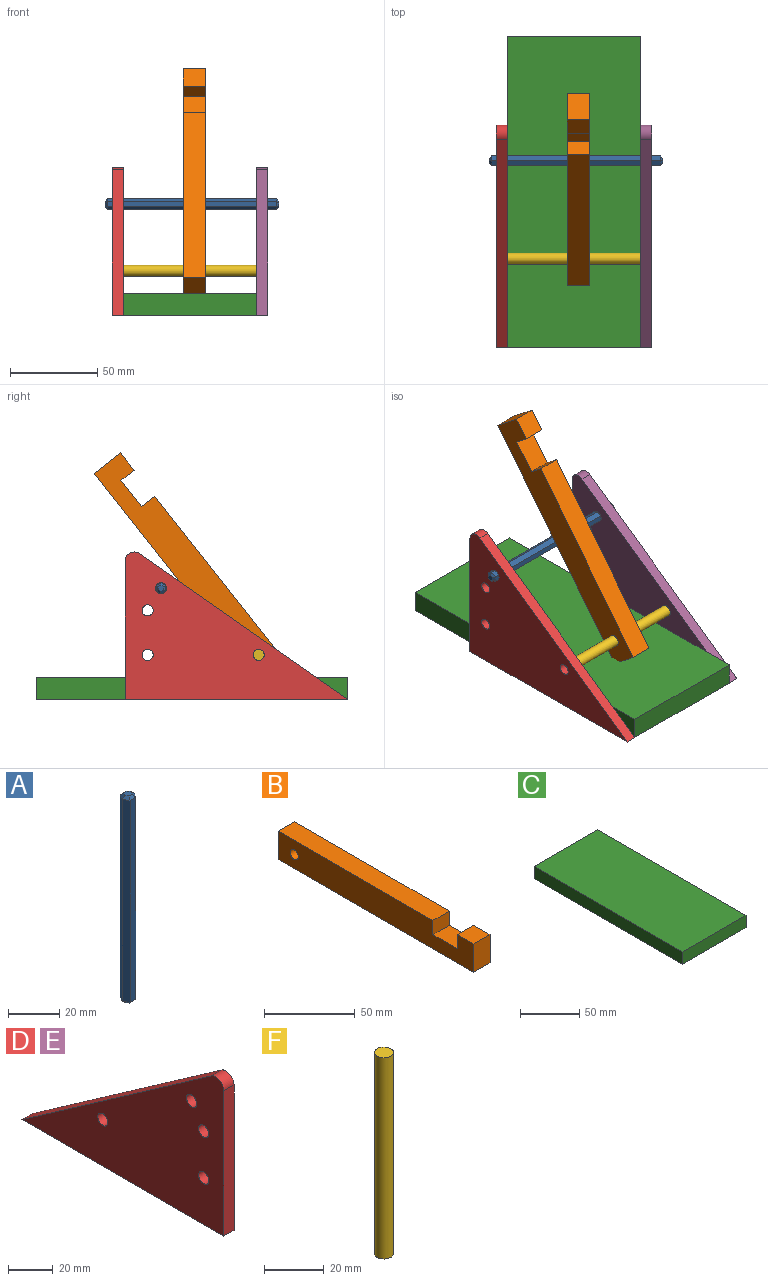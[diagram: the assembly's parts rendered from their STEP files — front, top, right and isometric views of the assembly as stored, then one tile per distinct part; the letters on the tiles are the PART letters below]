
ASSEMBLY  parts=6 mates=5
PART A: 20 faces, bbox 6.4x5.5x99.1 mm
  f0: plane 96.52x2.75mm, normal (0.87,-0.5,0), area 306.5mm2, adj f1,f5,f12,f18
  f1: plane 96.52x2.75mm, normal (0.87,0.5,0), area 306.5mm2, adj f0,f2,f13,f19
  f2: plane 96.52x3.18mm, normal (0,1,0), area 306.5mm2, adj f1,f3,f11,f17
  f3: plane 96.52x2.75mm, normal (-0.87,0.5,0), area 306.5mm2, adj f2,f4,f9,f15
  f4: plane 96.52x2.75mm, normal (-0.87,-0.5,0), area 306.5mm2, adj f3,f5,f8,f14
  f5: plane 96.52x3.18mm, normal (0,-1,0), area 306.5mm2, adj f0,f4,f10,f16
  f6: plane 3.42x2.96mm, normal (0,0,1), area 7.6mm2, adj f8,f9,f10,f11,f12,f13
  f7: plane 3.42x2.96mm, normal (0,0,-1), area 7.6mm2, adj f14,f15,f16,f17,f18,f19
  f8: plane 2.75x2.32mm, normal (-0.61,-0.35,0.71), area 4.4mm2, adj f4,f6,f9,f10
  f9: plane 2.75x2.32mm, normal (-0.61,0.35,0.71), area 4.4mm2, adj f3,f6,f8,f11
  f10: plane 3.18x1.27mm, normal (0,-0.71,0.71), area 4.4mm2, adj f5,f6,f8,f12
  f11: plane 3.18x1.27mm, normal (0,0.71,0.71), area 4.4mm2, adj f2,f6,f9,f13
  f12: plane 2.75x2.32mm, normal (0.61,-0.35,0.71), area 4.4mm2, adj f0,f6,f10,f13
  f13: plane 2.75x2.32mm, normal (0.61,0.35,0.71), area 4.4mm2, adj f1,f6,f11,f12
  f14: plane 2.75x2.32mm, normal (-0.61,-0.35,-0.71), area 4.4mm2, adj f4,f7,f15,f16
  f15: plane 2.75x2.32mm, normal (-0.61,0.35,-0.71), area 4.4mm2, adj f3,f7,f14,f17
  f16: plane 3.18x1.27mm, normal (0,-0.71,-0.71), area 4.4mm2, adj f5,f7,f14,f18
  f17: plane 3.18x1.27mm, normal (0,0.71,-0.71), area 4.4mm2, adj f2,f7,f15,f19
  f18: plane 2.75x2.32mm, normal (0.61,-0.35,-0.71), area 4.4mm2, adj f0,f7,f16,f19
  f19: plane 2.75x2.32mm, normal (0.61,0.35,-0.71), area 4.4mm2, adj f1,f7,f17,f18
PART B: 11 faces, bbox 12.7x152.4x19.1 mm
  f0: plane 19.05x12.7mm, normal (0,1,0), area 241.9mm2, adj f1,f8,f9,f10
  f1: plane 120.65x12.7mm, normal (0,0,1), area 1532.3mm2, adj f0,f2,f9,f10
  f2: plane 12.7x9.53mm, normal (0,-1,0), area 121mm2, adj f1,f3,f9,f10
  f3: plane 19.05x12.7mm, normal (0,0,1), area 241.9mm2, adj f2,f4,f9,f10
  f4: plane 12.7x9.53mm, normal (0,1,0), area 121mm2, adj f3,f5,f9,f10
  f5: plane 12.7x12.7mm, normal (0,0,1), area 161.3mm2, adj f4,f6,f9,f10
  f6: plane 19.05x12.7mm, normal (0,-1,0), area 241.9mm2, adj f5,f8,f9,f10
  f7: cylinder r=3.2mm len=12.7mm, axis (-1,0,0), area 255.4mm2, adj f9,f10
  f8: plane 152.4x12.7mm, normal (0,0,-1), area 1935.5mm2, adj f0,f6,f9,f10
  f9: plane 152.4x19.05mm, normal (1,0,0), area 2689.6mm2, adj f0,f1,f2,f3,f4,f5,f6,f7
  f10: plane 152.4x19.05mm, normal (-1,0,0), area 2689.6mm2, adj f0,f1,f2,f3,f4,f5,f6,f7
PART C: 6 faces, bbox 76.2x177.8x12.7 mm
  f0: plane 76.2x12.7mm, normal (0,-1,0), area 967.7mm2, adj f1,f3,f4,f5
  f1: plane 177.8x12.7mm, normal (1,0,0), area 2258.1mm2, adj f0,f2,f4,f5
  f2: plane 76.2x12.7mm, normal (0,1,0), area 967.7mm2, adj f1,f3,f4,f5
  f3: plane 177.8x12.7mm, normal (-1,0,0), area 2258.1mm2, adj f0,f2,f4,f5
  f4: plane 177.8x76.2mm, normal (0,0,1), area 13548.4mm2, adj f0,f1,f2,f3
  f5: plane 177.8x76.2mm, normal (0,0,-1), area 13548.4mm2, adj f0,f1,f2,f3
PART D: 10 faces, bbox 6.4x127x84.2 mm
  f0: plane 127x6.35mm, normal (0,0,-1), area 806.5mm2, adj f1,f5,f7,f8
  f1: plane 119.01x83.3mm, normal (0,0.57,0.82), area 922.4mm2, adj f0,f7,f8,f9
  f2: cylinder r=3.17mm len=6.35mm, axis (-1,0,0), area 126.7mm2, adj f7,f8
  f3: cylinder r=3.17mm len=6.35mm, axis (-1,0,0), area 126.7mm2, adj f7,f8
  f4: cylinder r=3.17mm len=6.35mm, axis (-1,0,0), area 126.7mm2, adj f7,f8
  f5: plane 79.14x6.35mm, normal (0,-1,0), area 502.6mm2, adj f0,f7,f8,f9
  f6: cylinder r=3.17mm len=6.35mm, axis (-1,0,0), area 126.7mm2, adj f7,f8
  f7: plane 127x84.22mm, normal (1,0,0), area 5497.1mm2, adj f0,f1,f2,f3,f4,f5,f6,f9
  f8: plane 127x84.22mm, normal (-1,0,0), area 5497.1mm2, adj f0,f1,f2,f3,f4,f5,f6,f9
  f9: cylinder r=5.08mm len=7.99mm, axis (-1,0,0), area 70.4mm2, adj f1,f5,f7,f8
PART E: same geometry as D
PART F: 3 faces, bbox 6.4x6.4x82.6 mm
  f0: cylinder r=3.17mm len=82.55mm, axis (0,0,-1), area 1646.8mm2, adj f1,f2
  f1: plane 6.35x6.35mm, normal (0,0,1), area 31.7mm2, adj f0
  f2: plane 6.35x6.35mm, normal (0,0,-1), area 31.7mm2, adj f0
PLACE A rot(axis=(0,-1,0),90deg) t=(63.76,17.78,67.1)mm
PLACE B rot(axis=(0,-0.44,0.9),180deg) t=(21.89,1.25,78.84)mm
PLACE C t=(13.15,0,3.6)mm fixed
PLACE D rot(axis=(0,0,1),180deg) t=(-24.95,-25.4,48.05)mm
PLACE E rot(axis=(0,0,1),180deg) t=(57.6,-25.4,48.05)mm
PLACE F rot(axis=(0,1,0),90deg) t=(-25.73,-38.1,29)mm fixed
MATE slider F.f0 <-> D.f6  axis (-1,0,0) through (15.54,-38.1,29)mm
MATE fastened E.f7 <-> C.f1  axis (-1,0,0) through (51.25,-88.9,3.6)mm
MATE fastened C.f3 <-> D.f8  axis (-1,0,0) through (-24.95,-88.9,3.6)mm
MATE slider E.f3 <-> A.f7  axis (1,0,0) through (57.6,17.78,67.1)mm
MATE revolute B.f7 <-> F.f0  axis (1,0,0) through (15.54,-38.1,29)mm
